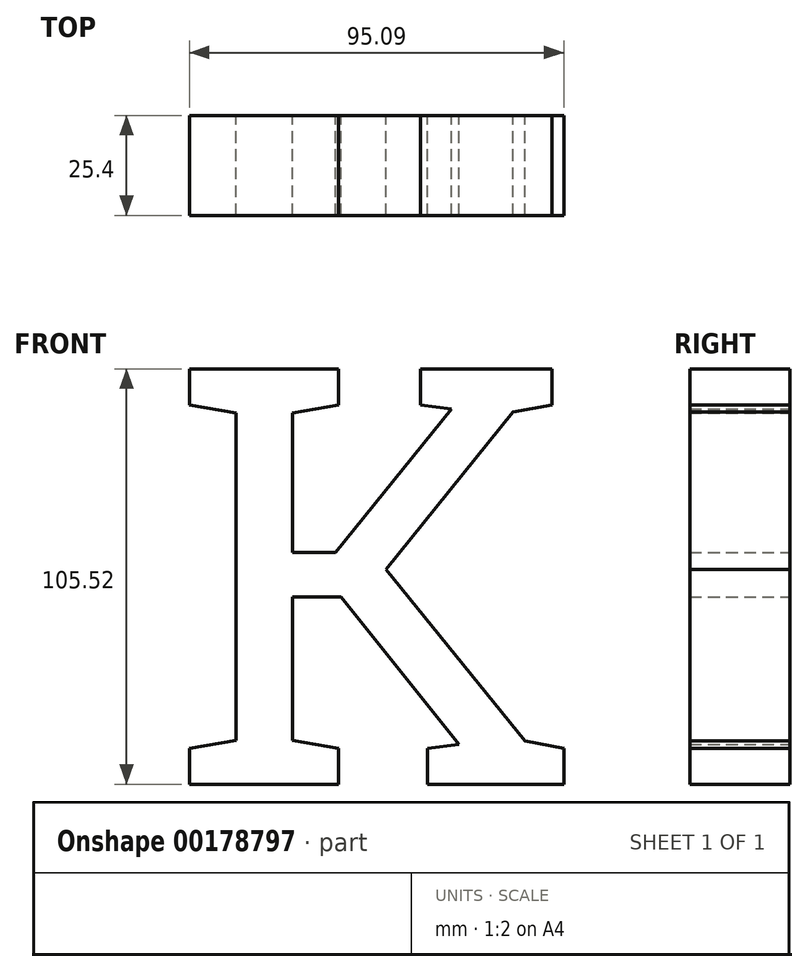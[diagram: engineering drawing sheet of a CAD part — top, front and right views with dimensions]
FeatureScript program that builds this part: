
annotation { "Feature Type Name" : "Feature", "Feature Type Description" : "" }
export const myFeature = defineFeature(function(context is Context, id is Id, definition is map)
    precondition{}
    {
        {
            var Q0;
            Q0=qCreatedBy(makeId("Front.planeOp"),FACE);
            var sketch = newSketch(context, id + "F0", { "sketchPlane" : qUnion([Q0])});
            skText(sketch, "E0", { "text": "K", "fontName": "RobotoSlab-Regular.ttf"});
            const initialGuessF0  = {"E0": [-0.04443, -0.05823, 1, 0, 0.10687]};
            skSetInitialGuess(sketch, initialGuessF0);
            skSolve(sketch);
        }
        {
            var Q0;
            Q0=makeQuery(id+"F0.imprint","IMPRINT",FACE,{"disambiguationData":[TD([[makeQuery(id+"F0.imprint","IMPRINT",EDGE,{"derivedFrom":sQuery(id+"F0.wireOp",EDGE,"E0.sketch_text.stroke-0")}),-1.0]])]});
            extrude(context, id + "F1", {"entities" : qUnion([Q0]), "depth" : 25.4 * mm});
        }
    });
